# Revit family: OglaendSystem_FOE_Tee-Piece_73L
name_source: partatom
category: Соединительные детали кабельных лотков
revit_build: Autodesk Revit 2018 (Build: 20170927_1515(x64)
units: mm (PartAtom-declared; Revit-internal decimal feet)

## family parameters
Всегда вертикально = Да
Заголовок OmniClass = Cable Trays and Horizontal Racks
На основе рабочей плоскости = Нет
Номер OmniClass = 23.80.30.17.17
Общий = Нет
При загрузке вырезать с полостями = Нет
Размер круглого соединителя = Использовать диаметр
Тип детали = Тройник ступенчатого

## types (2) — shared parameters
Рзм.Угол = 45.00°
Таблица выбора артикула = FOE TE FRP A
Таблица выбора массы = FOE TE FRP W
Таблица выбора наименования = FOE TE FRP N
Таблица выбора типа = FOE TE FRP T
Тип.КрышкаЛотка = OglaendSystem_FOE_Cover_TeePiece_96L : Исполнение FRP

## per-type parameters (varying)
| type | Рзм.R2 |
| Исполнение FRP. Радиус загиба 300мм. | 300 мм |
| Исполнение FRP. Радиус загиба 600мм. | 600 мм |

## geometry (parser evidence)
native form markers: Blend x2
no freeform markers — native parametric forms only
